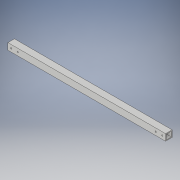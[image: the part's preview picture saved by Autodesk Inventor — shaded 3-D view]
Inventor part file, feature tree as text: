
AUTODESK INVENTOR PART (.ipt)
format: ipt  version: 2018 (Build 220112000, 112)  size: 121,344 bytes
history: native  units: in
note: dims shown in document units (in); Inventor stores cm internally (conversion verified against a paired STEP export)
features: extrude x2, sketch x2
ambient origin geometry x8: Origin, YZ Plane, XZ Plane, XY Plane, X Axis, Y Axis, Z Axis, Center Point
bodies: Solid1 (feature_tree)
feature tree (4):
  extrude  "Extrusion1"  Depth=1.0in
  extrude  "Extrusion3"  Depth=24.0in TaperAngle=0.0deg
  sketch  "Sketch1"  dims[d0=1.0in d1=1.0in]
  sketch  "Sketch3"  dims[d2=0.125in d3=24.0in d4=0.0in d7=0.5in d8=1.0in d9=0.5in d10=1.0in d11=0.2031in d12=0.2031in d13=0.2031in d14=0.2031in d15=23.0in d16=0.0in]
